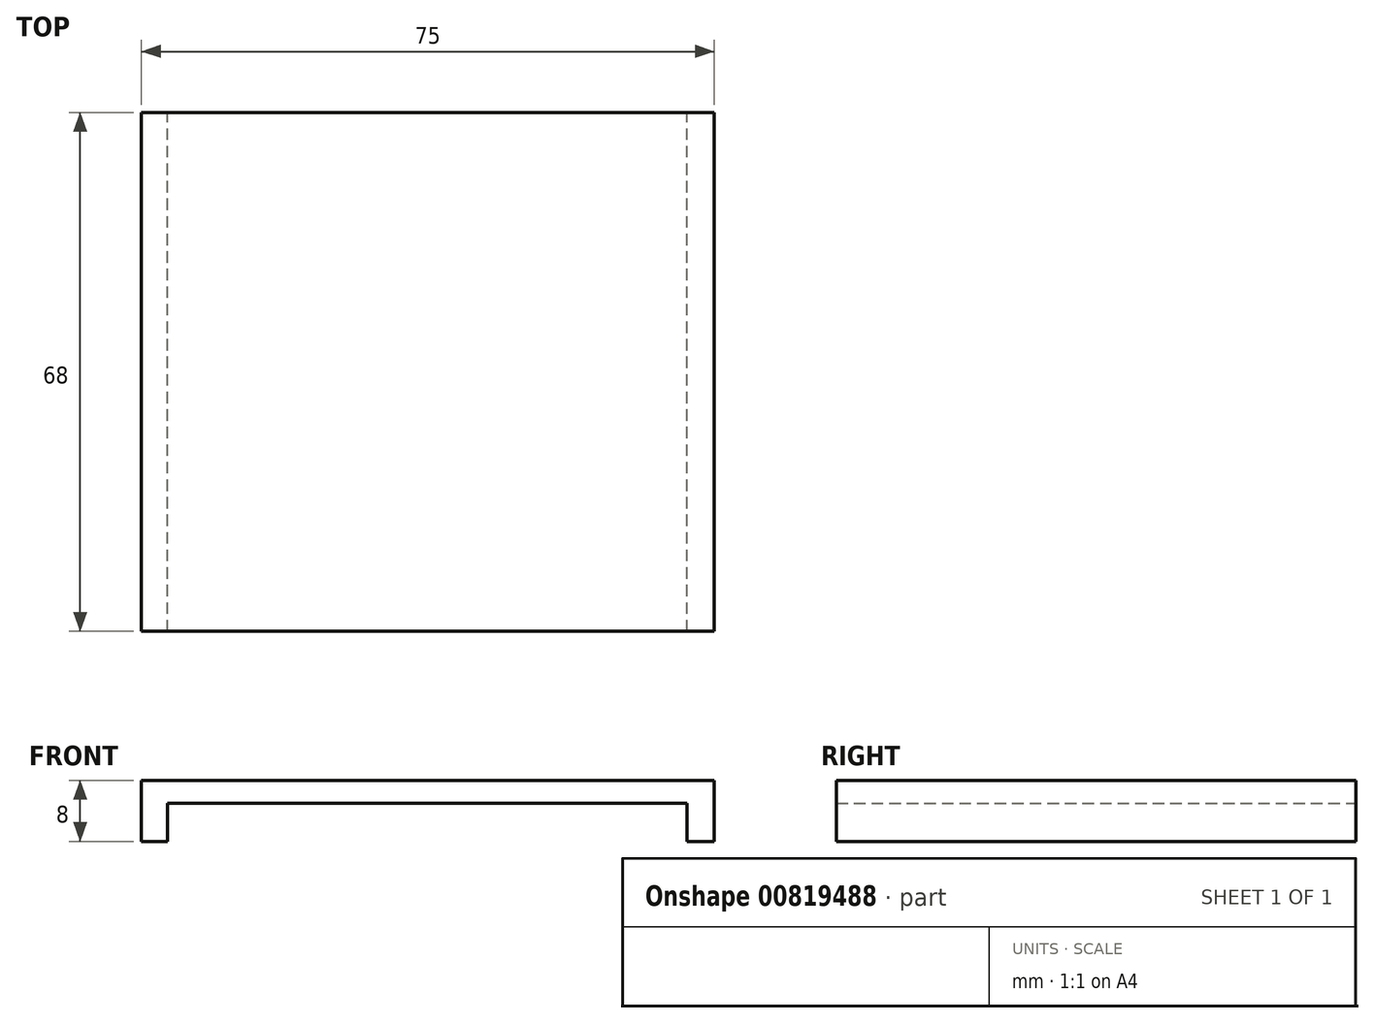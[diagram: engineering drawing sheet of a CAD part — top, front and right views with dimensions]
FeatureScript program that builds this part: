
annotation { "Feature Type Name" : "Feature", "Feature Type Description" : "" }
export const myFeature = defineFeature(function(context is Context, id is Id, definition is map)
    precondition{}
    {
        {
            var Q0;
            Q0=qCreatedBy(makeId("Top.planeOp"),FACE);
            var sketch = newSketch(context, id + "F0", { "sketchPlane" : qUnion([Q0])});
            skLineSegment(sketch, "E0.bottom", {"start": v(37.5, -34) * mm, "end": v(-37.5, -34) * mm});
            skLineSegment(sketch, "E0.top", {"start": v(37.5, 34) * mm, "end": v(-37.5, 34) * mm});
            skLineSegment(sketch, "E0.left", {"start": v(37.5, -34) * mm, "end": v(37.5, 34) * mm});
            skLineSegment(sketch, "E0.right", {"start": v(-37.5, -34) * mm, "end": v(-37.5, 34) * mm});
            skPoint(sketch, "E0.middle", {"position": v(0, 0) * mm});
            skSolve(sketch);
        }
        {
            var Q0;
            Q0=makeQuery(id+"F0.imprint","IMPRINT",FACE,{"disambiguationData":[TD([[makeQuery(id+"F0.imprint","IMPRINT",EDGE,{"derivedFrom":sQuery(id+"F0.wireOp",EDGE,"E0.bottom")}),-1.0]])]});
            extrude(context, id + "F1", {"entities" : qUnion([Q0]), "depth" : 3 * mm, "offsetDistance" : 25 * mm});
        }
        {
            var Q0;
            Q0=makeQuery(id+"F1.opExtrude","CAP_FACE",FACE,{"disambiguationData":[OSD([sQuery(id+"F0.wireOp",EDGE,"E0.bottom"),sQuery(id+"F0.wireOp",EDGE,"E0.top"),sQuery(id+"F0.wireOp",EDGE,"E0.left"),sQuery(id+"F0.wireOp",EDGE,"E0.right")])],"isStart":true});
            var sketch = newSketch(context, id + "F2", { "sketchPlane" : qUnion([Q0])});
            skLineSegment(sketch, "E1", {"start": v(-34.06, 34) * mm, "end": v(-34.06, -34) * mm});
            skSolve(sketch);
        }
        {
            var Q0;
            {var subQ0=sQuery(id+"F2.wireOp",EDGE,"E1");Q0=makeQuery(id+"F2.imprint","IMPRINT",FACE,{"disambiguationData":[TD([[makeQuery(id+"F2.imprint","IMPRINT",EDGE,{"derivedFrom":subQ0}),1.0]])]});}
            var sketch = newSketch(context, id + "F3", { "sketchPlane" : qUnion([Q0])});
            skLineSegment(sketch, "E2", {"start": v(33.9, 34.91) * mm, "end": v(33.9, -34.98) * mm});
            skSolve(sketch);
        }
        {
            var Q0;
            {var subQ0=sQuery(id+"F2.wireOp",EDGE,"E1");Q0=makeQuery(id+"F2.imprint","IMPRINT",FACE,{"disambiguationData":[TD([[makeQuery(id+"F2.imprint","IMPRINT",EDGE,{"derivedFrom":subQ0}),-1.0]])]});}
            var Q1;
            {var subQ1=makeQuery(id+"F1.opExtrude","CAP_EDGE",EDGE,{"disambiguationData":[OSD([sQuery(id+"F0.wireOp",EDGE,"E0.left")])],"isStart":true});var subQ9=makeQuery(id+"F2.imprint","IMPRINT",EDGE,{"derivedFrom":subQ1});Q1=makeQuery(id+"F3.imprint","IMPRINT",FACE,{"disambiguationData":[TD([[makeQuery(id+"F3.imprint","IMPRINT",EDGE,{"derivedFrom":subQ9}),-1.0]])]});}
            extrude(context, id + "F4", {"entities" : qUnion([Q0, Q1]), "operationType" : NewBodyOperationType.ADD, "depth" : 5 * mm, "offsetDistance" : 25 * mm});
        }
    });
